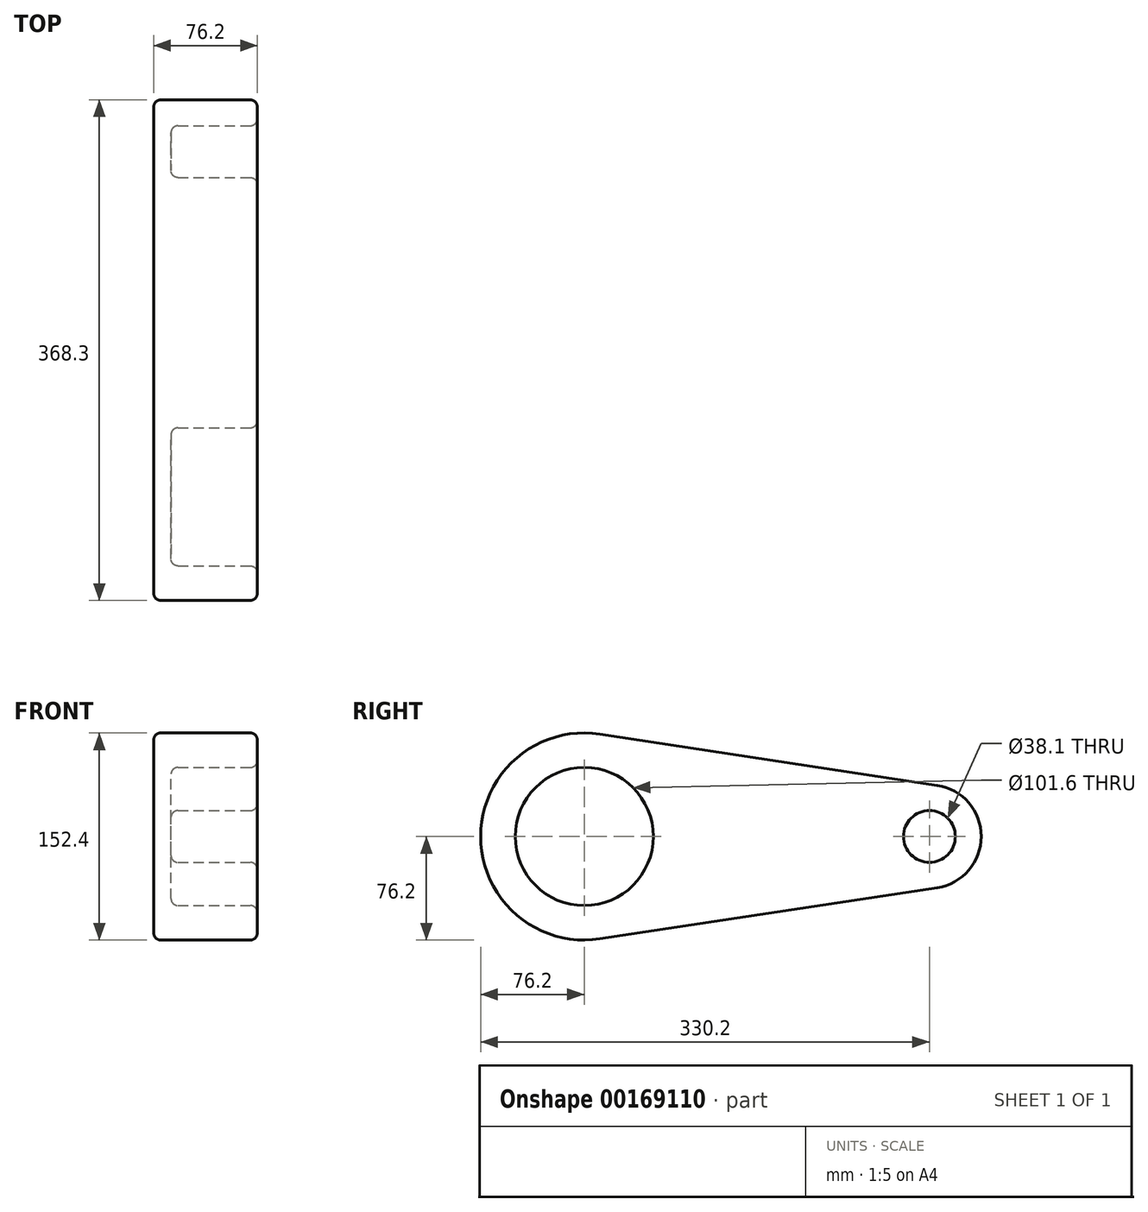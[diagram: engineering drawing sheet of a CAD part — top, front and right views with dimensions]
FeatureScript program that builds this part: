
annotation { "Feature Type Name" : "Feature", "Feature Type Description" : "" }
export const myFeature = defineFeature(function(context is Context, id is Id, definition is map)
    precondition{}
    {
        {
            var Q0;
            Q0=qCreatedBy(makeId("Right.planeOp"),FACE);
            var sketch = newSketch(context, id + "F3", { "sketchPlane" : qUnion([Q0])});
            skCircle(sketch, "E0", {"center": v(0, 0) * mm, "radius": 76.2 * mm});
            skCircle(sketch, "E1", {"center": v(254, 0) * mm, "radius": 38.1 * mm});
            skLineSegment(sketch, "E2", {"start": v(259.72, 37.67) * mm, "end": v(11.43, 75.34) * mm});
            skLineSegment(sketch, "E3", {"start": v(259.72, -37.67) * mm, "end": v(11.43, -75.34) * mm});
            skSolve(sketch);
        }
        {
            var Q0;
            {var subQ0=sQuery(id+"F3.wireOp",EDGE,"E2");Q0=makeQuery(id+"F3.imprint","IMPRINT",FACE,{"disambiguationData":[TD([[makeQuery(id+"F3.imprint","IMPRINT",EDGE,{"derivedFrom":subQ0}),1.0]])]});}
            var Q1;
            {var subQ0=sQuery(id+"F3.wireOp",EDGE,"E0");var subQ1=makeQuery(id+"F3.imprint","INTERSECT",VERTEX,{"derivedFrom":[subQ0,sQuery(id+"F3.wireOp",EDGE,"E2")]});Q1=makeQuery(id+"F3.imprint","IMPRINT",FACE,{"disambiguationData":[TD([[makeQuery(id+"F3.imprint","IMPRINT",EDGE,{"disambiguationData":[TD([[subQ1,-1.0]])],"derivedFrom":subQ0}),1.0]])]});}
            var Q2;
            {var subQ0=sQuery(id+"F3.wireOp",EDGE,"E1");var subQ1=makeQuery(id+"F3.imprint","INTERSECT",VERTEX,{"derivedFrom":[subQ0,sQuery(id+"F3.wireOp",EDGE,"E2")]});Q2=makeQuery(id+"F3.imprint","IMPRINT",FACE,{"disambiguationData":[TD([[makeQuery(id+"F3.imprint","IMPRINT",EDGE,{"disambiguationData":[TD([[subQ1,-1.0]])],"derivedFrom":subQ0}),1.0]])]});}
            extrude(context, id + "F4", {"entities" : qUnion([Q0, Q1, Q2]), "endBound" : BoundingType.SYMMETRIC, "depth" : 76.2 * mm});
        }
        {
            var Q0;
            Q0=makeQuery(id+"F4.opExtrude","CAP_FACE",FACE,{"disambiguationData":[OSD([sQuery(id+"F3.wireOp",EDGE,"E0"),sQuery(id+"F3.wireOp",EDGE,"E1"),sQuery(id+"F3.wireOp",EDGE,"E2"),sQuery(id+"F3.wireOp",EDGE,"E3")])],"isStart":false});
            var sketch = newSketch(context, id + "F0", { "sketchPlane" : qUnion([Q0])});
            skCircle(sketch, "E4", {"center": v(0, 0) * mm, "radius": 50.8 * mm});
            skCircle(sketch, "E5", {"center": v(254, 0) * mm, "radius": 19.05 * mm});
            skSolve(sketch);
        }
        {
            var Q0;
            Q0=makeQuery(id+"F0.imprint","IMPRINT",FACE,{"disambiguationData":[TD([[makeQuery(id+"F0.imprint","IMPRINT",EDGE,{"derivedFrom":sQuery(id+"F0.wireOp",EDGE,"E4")}),1.0]])]});
            var Q1;
            Q1=makeQuery(id+"F0.imprint","IMPRINT",FACE,{"disambiguationData":[TD([[makeQuery(id+"F0.imprint","IMPRINT",EDGE,{"derivedFrom":sQuery(id+"F0.wireOp",EDGE,"E5")}),1.0]])]});
            extrude(context, id + "F1", {"entities" : qUnion([Q0, Q1]), "operationType" : NewBodyOperationType.REMOVE, "oppositeDirection" : true, "depth" : 63.5 * mm});
        }
        {
            var Q0;
            Q0=makeQuery(id+"F4.opExtrude","CAP_FACE",FACE,{"disambiguationData":[OSD([sQuery(id+"F3.wireOp",EDGE,"E0"),sQuery(id+"F3.wireOp",EDGE,"E1"),sQuery(id+"F3.wireOp",EDGE,"E2"),sQuery(id+"F3.wireOp",EDGE,"E3")])],"isStart":false});
            fillet(context, id + "F5", {"entities" : qUnion([Q0]), "radius" : 5.08 * mm, "tangentPropagation" : true, "allowEdgeOverflow" : false});
        }
        {
            var Q0;
            Q0=makeQuery(id+"F1.boolean.opBoolean","COPY",FACE,{"derivedFrom":makeQuery(id+"F1.opExtrude","SWEPT_FACE",FACE,{"disambiguationData":[OSD([sQuery(id+"F0.wireOp",EDGE,"E4")])]})});
            var Q1;
            Q1=makeQuery(id+"F1.boolean.opBoolean","COPY",EDGE,{"derivedFrom":makeQuery(id+"F1.opExtrude","CAP_EDGE",EDGE,{"disambiguationData":[OSD([sQuery(id+"F0.wireOp",EDGE,"E4")])],"isStart":false})});
            var Q2;
            Q2=makeQuery(id+"F4.opExtrude","CAP_FACE",FACE,{"disambiguationData":[OSD([sQuery(id+"F3.wireOp",EDGE,"E0"),sQuery(id+"F3.wireOp",EDGE,"E1"),sQuery(id+"F3.wireOp",EDGE,"E2"),sQuery(id+"F3.wireOp",EDGE,"E3")])],"isStart":true});
            var Q3;
            {var subQ0=sQuery(id+"F0.wireOp",EDGE,"E5");Q3=makeQuery(id+"F5.opFillet","BLEND_EDGE",EDGE,{"blendedFrom":[makeQuery(id+"F1.boolean.opBoolean","COPY",EDGE,{"derivedFrom":makeQuery(id+"F1.opExtrude","CAP_EDGE",EDGE,{"disambiguationData":[OSD([subQ0])],"isStart":true})}),makeQuery(id+"F1.boolean.opBoolean","COPY",FACE,{"derivedFrom":makeQuery(id+"F1.opExtrude","SWEPT_FACE",FACE,{"disambiguationData":[OSD([subQ0])]})})],"blendedInto":[makeQuery(id+"F1.boolean.opBoolean","COPY",FACE,{"derivedFrom":makeQuery(id+"F1.opExtrude","SWEPT_FACE",FACE,{"disambiguationData":[OSD([subQ0])]})})]});}
            var Q4;
            Q4=makeQuery(id+"F1.boolean.opBoolean","COPY",EDGE,{"derivedFrom":makeQuery(id+"F1.opExtrude","CAP_EDGE",EDGE,{"disambiguationData":[OSD([sQuery(id+"F0.wireOp",EDGE,"E5")])],"isStart":false})});
            fillet(context, id + "F2", {"entities" : qUnion([Q0, Q1, Q2, Q3, Q4]), "radius" : 5.08 * mm, "tangentPropagation" : true, "allowEdgeOverflow" : false});
        }
    });
